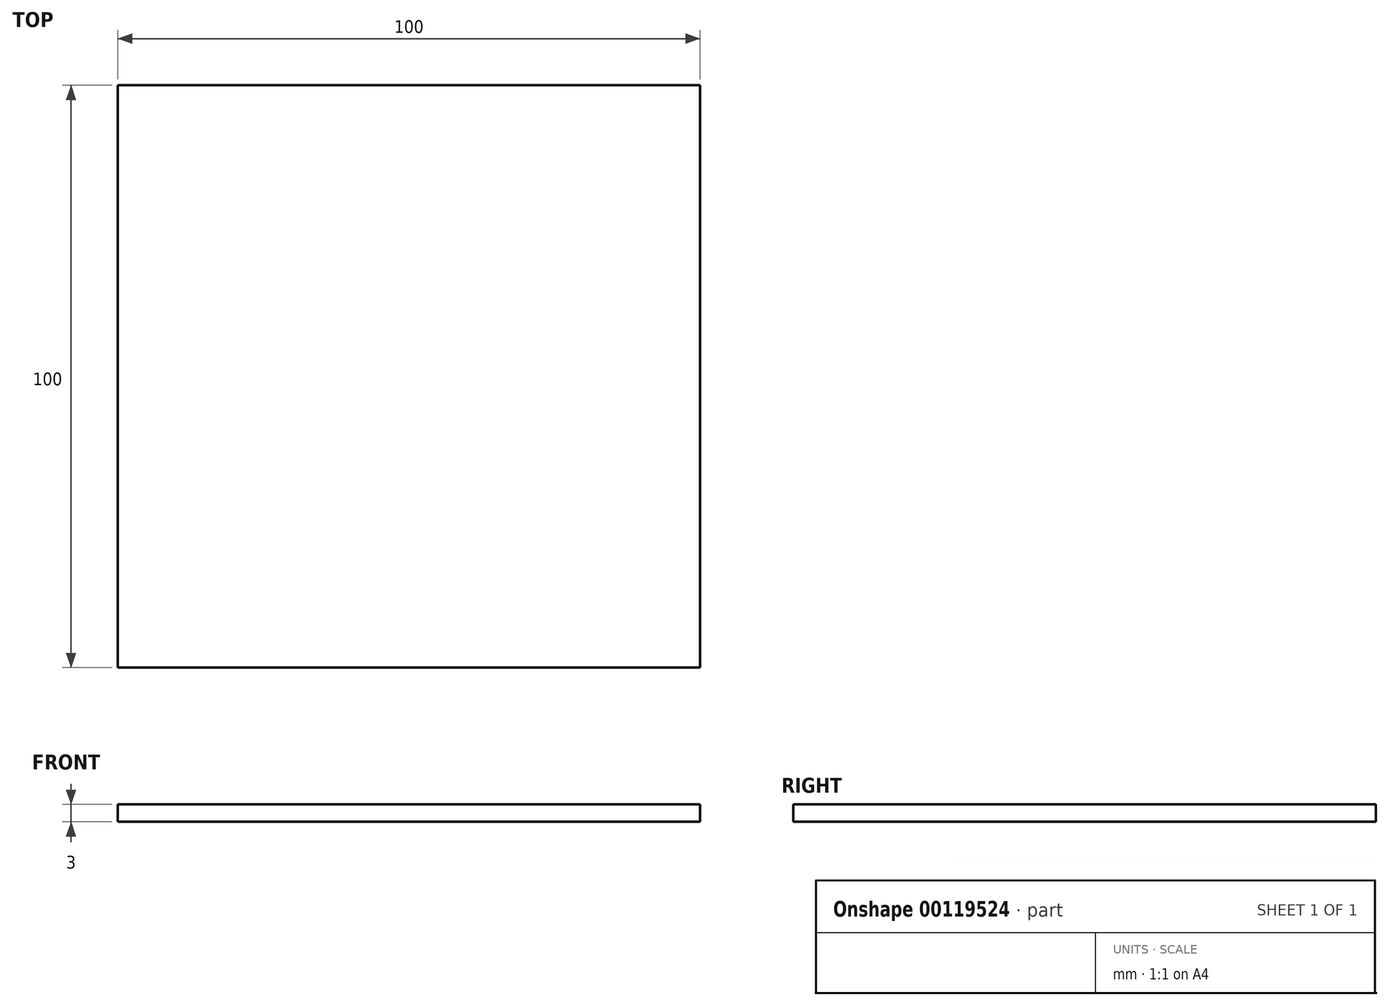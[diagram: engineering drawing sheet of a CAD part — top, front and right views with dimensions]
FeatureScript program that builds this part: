
annotation { "Feature Type Name" : "Feature", "Feature Type Description" : "" }
export const myFeature = defineFeature(function(context is Context, id is Id, definition is map)
    precondition{}
    {
        {
            var Q0;
            Q0=qCreatedBy(makeId("Top.planeOp"),FACE);
            var sketch = newSketch(context, id + "F0", { "sketchPlane" : qUnion([Q0])});
            skLineSegment(sketch, "E0.bottom", {"start": v(-50, -50) * mm, "end": v(50, -50) * mm});
            skLineSegment(sketch, "E0.top", {"start": v(-50, 50) * mm, "end": v(50, 50) * mm});
            skLineSegment(sketch, "E0.left", {"start": v(-50, -50) * mm, "end": v(-50, 50) * mm});
            skLineSegment(sketch, "E0.right", {"start": v(50, -50) * mm, "end": v(50, 50) * mm});
            skPoint(sketch, "E0.middle", {"position": v(0, 0) * mm});
            skSolve(sketch);
        }
        {
            var Q0;
            Q0=makeQuery(id+"F0.imprint","IMPRINT",FACE,{"disambiguationData":[TD([[makeQuery(id+"F0.imprint","IMPRINT",EDGE,{"derivedFrom":sQuery(id+"F0.wireOp",EDGE,"E0.bottom")}),1.0]])]});
            extrude(context, id + "F1", {"entities" : qUnion([Q0]), "depth" : 3 * mm});
        }
    });
